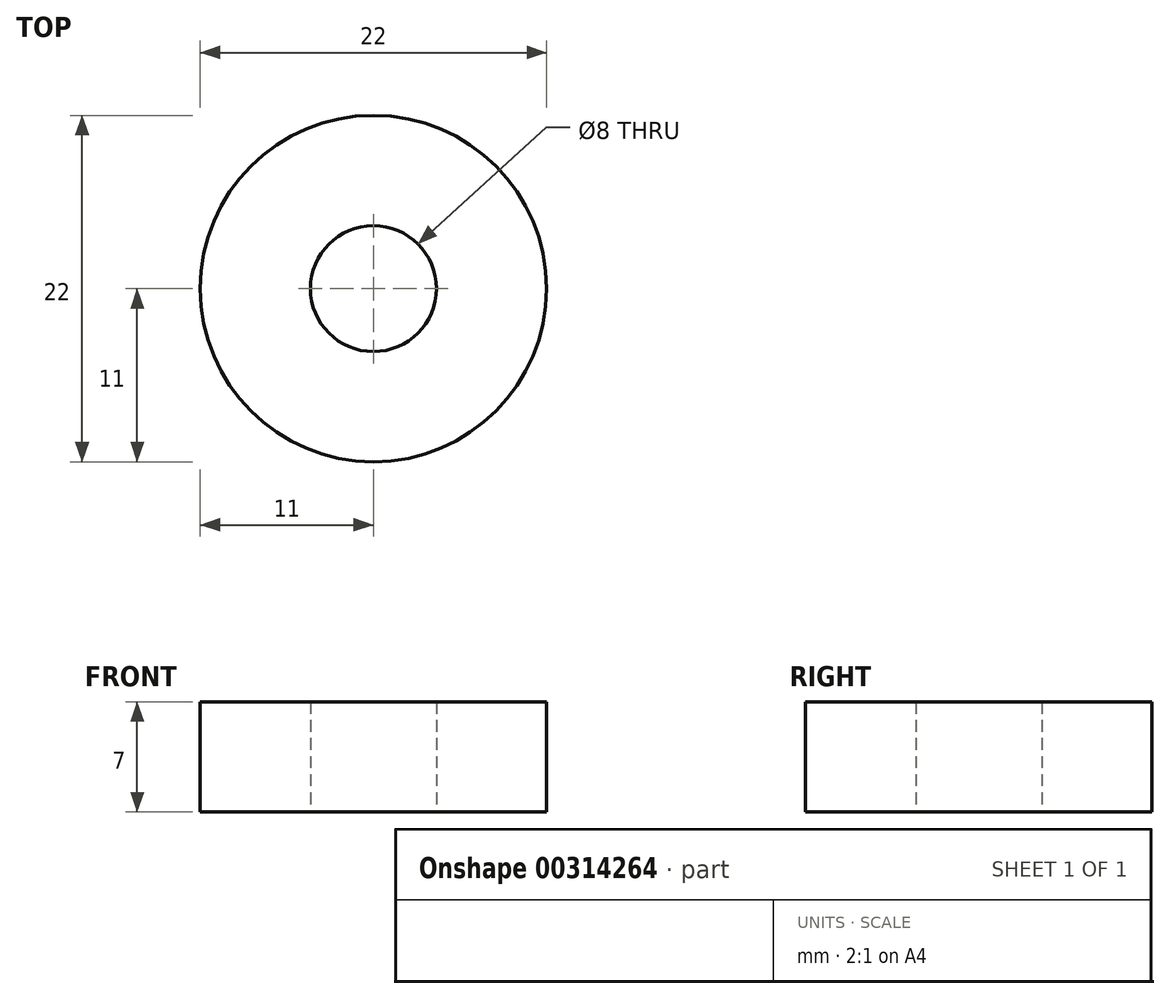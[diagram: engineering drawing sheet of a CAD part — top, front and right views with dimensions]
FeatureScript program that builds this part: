
annotation { "Feature Type Name" : "Feature", "Feature Type Description" : "" }
export const myFeature = defineFeature(function(context is Context, id is Id, definition is map)
    precondition{}
    {
        {
            var Q0;
            Q0=qCreatedBy(makeId("Top.planeOp"),FACE);
            var sketch = newSketch(context, id + "F0", { "sketchPlane" : qUnion([Q0])});
            skCircle(sketch, "E0", {"center": v(0, 0) * mm, "radius": 4 * mm});
            skCircle(sketch, "E1", {"center": v(0, 0) * mm, "radius": 11 * mm});
            skSolve(sketch);
        }
        {
            var Q0;
            Q0 = qSketchRegion(id + "F0", true);
            extrude(context, id + "F1", {"entities" : qUnion([Q0]), "depth" : 7 * mm});
        }
    });
